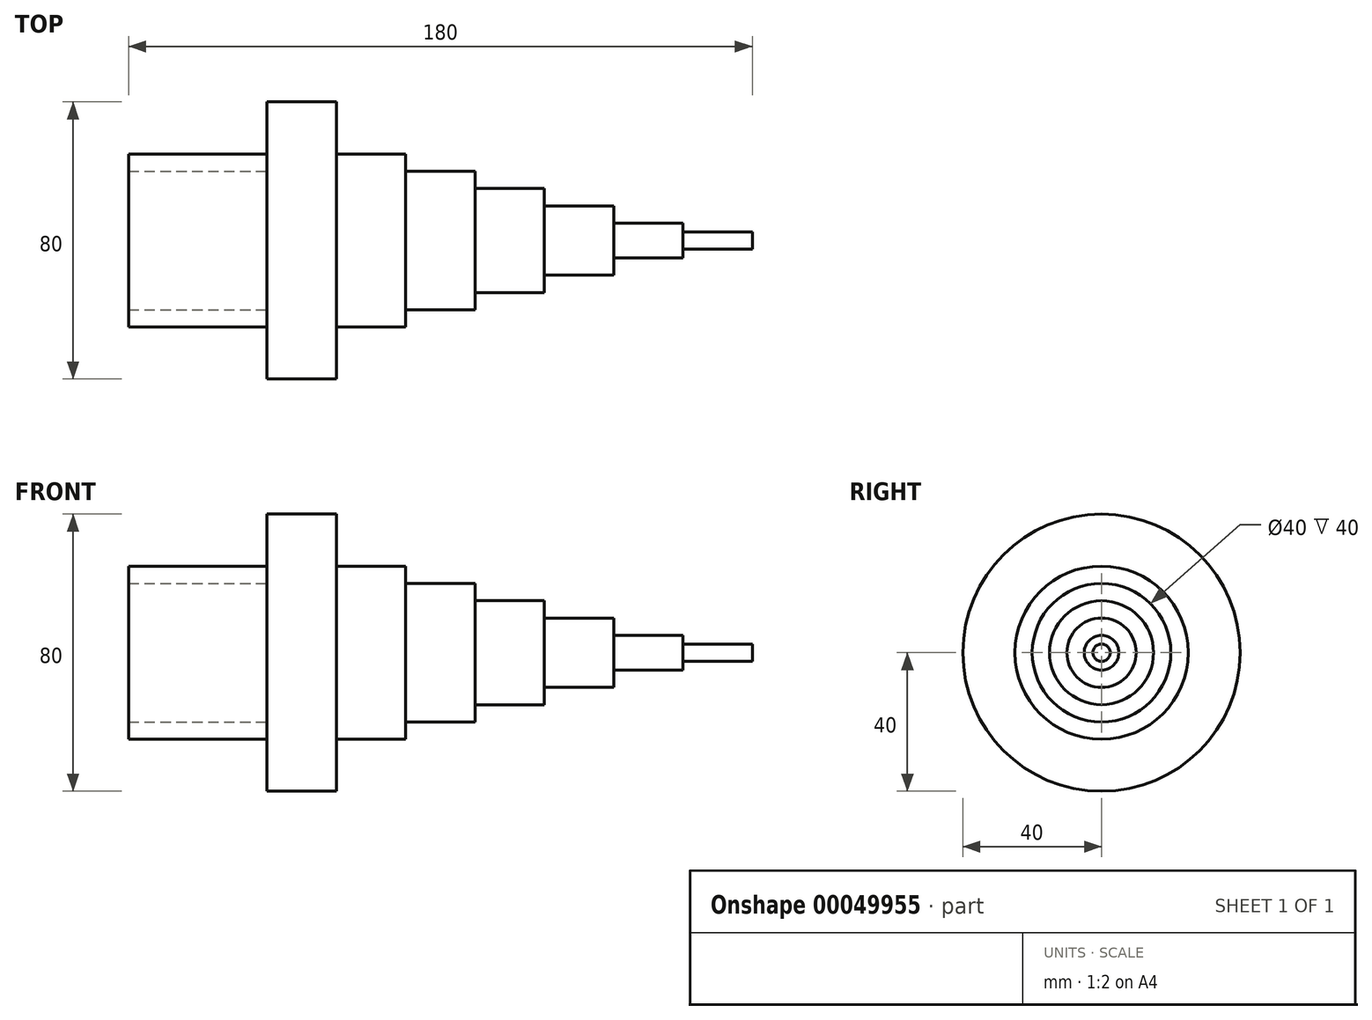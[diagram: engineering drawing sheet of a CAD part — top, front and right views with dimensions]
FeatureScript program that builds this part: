
annotation { "Feature Type Name" : "Feature", "Feature Type Description" : "" }
export const myFeature = defineFeature(function(context is Context, id is Id, definition is map)
    precondition{}
    {
        {
            var Q0;
            Q0=qCreatedBy(makeId("Front.planeOp"),FACE);
            var sketch = newSketch(context, id + "F0", { "sketchPlane" : qUnion([Q0])});
            skLineSegment(sketch, "E0", {"start": v(0, 0) * mm, "end": v(0, 25) * mm});
            skLineSegment(sketch, "E1", {"start": v(0, 25) * mm, "end": v(40, 25) * mm});
            skLineSegment(sketch, "E2", {"start": v(40, 25) * mm, "end": v(40, 40) * mm});
            skLineSegment(sketch, "E3", {"start": v(40, 40) * mm, "end": v(60, 40) * mm});
            skLineSegment(sketch, "E4", {"start": v(60, 40) * mm, "end": v(60, 25) * mm});
            skLineSegment(sketch, "E5", {"start": v(60, 25) * mm, "end": v(80, 25) * mm});
            skLineSegment(sketch, "E6", {"start": v(80, 25) * mm, "end": v(80, 20) * mm});
            skLineSegment(sketch, "E7", {"start": v(80, 20) * mm, "end": v(100, 20) * mm});
            skLineSegment(sketch, "E8", {"start": v(100, 20) * mm, "end": v(100, 15) * mm});
            skLineSegment(sketch, "E9", {"start": v(100, 15) * mm, "end": v(120, 15) * mm});
            skLineSegment(sketch, "E10", {"start": v(120, 15) * mm, "end": v(120, 10) * mm});
            skLineSegment(sketch, "E11", {"start": v(120, 10) * mm, "end": v(140, 10) * mm});
            skLineSegment(sketch, "E12", {"start": v(140, 10) * mm, "end": v(140, 5) * mm});
            skLineSegment(sketch, "E13", {"start": v(140, 5) * mm, "end": v(160, 5) * mm});
            skLineSegment(sketch, "E14", {"start": v(160, 5) * mm, "end": v(160, 2.5) * mm});
            skLineSegment(sketch, "E15", {"start": v(160, 2.5) * mm, "end": v(180, 2.5) * mm});
            skLineSegment(sketch, "E16", {"start": v(180, 2.5) * mm, "end": v(180, 0) * mm});
            skLineSegment(sketch, "E17", {"start": v(180, 0) * mm, "end": v(0, 0) * mm});
            skLineSegment(sketch, "E18", {"start": v(40, 25) * mm, "end": v(40, 0) * mm});
            skLineSegment(sketch, "E19", {"start": v(60, 25) * mm, "end": v(60, 0) * mm});
            skLineSegment(sketch, "E20", {"start": v(80, 20) * mm, "end": v(80, 0) * mm});
            skLineSegment(sketch, "E21", {"start": v(100, 15) * mm, "end": v(100, 0) * mm});
            skLineSegment(sketch, "E22", {"start": v(120, 10) * mm, "end": v(120, 0) * mm});
            skLineSegment(sketch, "E23", {"start": v(140, 5) * mm, "end": v(140, 0) * mm});
            skLineSegment(sketch, "E24", {"start": v(160, 2.5) * mm, "end": v(160, 0) * mm});
            skLineSegment(sketch, "E25", {"start": v(0, 20) * mm, "end": v(40, 20) * mm});
            skSolve(sketch);
        }
        {
            var Q0;
            {var subQ2=sQuery(id+"F0.wireOp",EDGE,"E1");Q0=makeQuery(id+"F0.imprint","IMPRINT",FACE,{"disambiguationData":[TD([[makeQuery(id+"F0.imprint","IMPRINT",EDGE,{"derivedFrom":subQ2}),-1.0]])]});}
            var Q1;
            {var subQ5=sQuery(id+"F0.wireOp",EDGE,"E2");Q1=makeQuery(id+"F0.imprint","IMPRINT",FACE,{"disambiguationData":[TD([[makeQuery(id+"F0.imprint","IMPRINT",EDGE,{"derivedFrom":subQ5}),-1.0]])]});}
            var Q2;
            Q2=makeQuery(id+"F0.imprint","IMPRINT",FACE,{"disambiguationData":[TD([[makeQuery(id+"F0.imprint","IMPRINT",EDGE,{"derivedFrom":sQuery(id+"F0.wireOp",EDGE,"E5")}),-1.0]])]});
            var Q3;
            Q3=makeQuery(id+"F0.imprint","IMPRINT",FACE,{"disambiguationData":[TD([[makeQuery(id+"F0.imprint","IMPRINT",EDGE,{"derivedFrom":sQuery(id+"F0.wireOp",EDGE,"E7")}),-1.0]])]});
            var Q4;
            Q4=makeQuery(id+"F0.imprint","IMPRINT",FACE,{"disambiguationData":[TD([[makeQuery(id+"F0.imprint","IMPRINT",EDGE,{"derivedFrom":sQuery(id+"F0.wireOp",EDGE,"E9")}),-1.0]])]});
            var Q5;
            Q5=makeQuery(id+"F0.imprint","IMPRINT",FACE,{"disambiguationData":[TD([[makeQuery(id+"F0.imprint","IMPRINT",EDGE,{"derivedFrom":sQuery(id+"F0.wireOp",EDGE,"E11")}),-1.0]])]});
            var Q6;
            Q6=makeQuery(id+"F0.imprint","IMPRINT",FACE,{"disambiguationData":[TD([[makeQuery(id+"F0.imprint","IMPRINT",EDGE,{"derivedFrom":sQuery(id+"F0.wireOp",EDGE,"E13")}),-1.0]])]});
            var Q7;
            Q7=makeQuery(id+"F0.imprint","IMPRINT",FACE,{"disambiguationData":[TD([[makeQuery(id+"F0.imprint","IMPRINT",EDGE,{"derivedFrom":sQuery(id+"F0.wireOp",EDGE,"E15")}),-1.0]])]});
            var Q8;
            Q8=sQuery(id+"F0.wireOp",EDGE,"E17");
            revolve(context, id + "F1", {"entities" : qUnion([Q0, Q1, Q2, Q3, Q4, Q5, Q6, Q7]), "axis" : qUnion([Q8]), "revolveType" : RevolveType.FULL});
        }
    });
